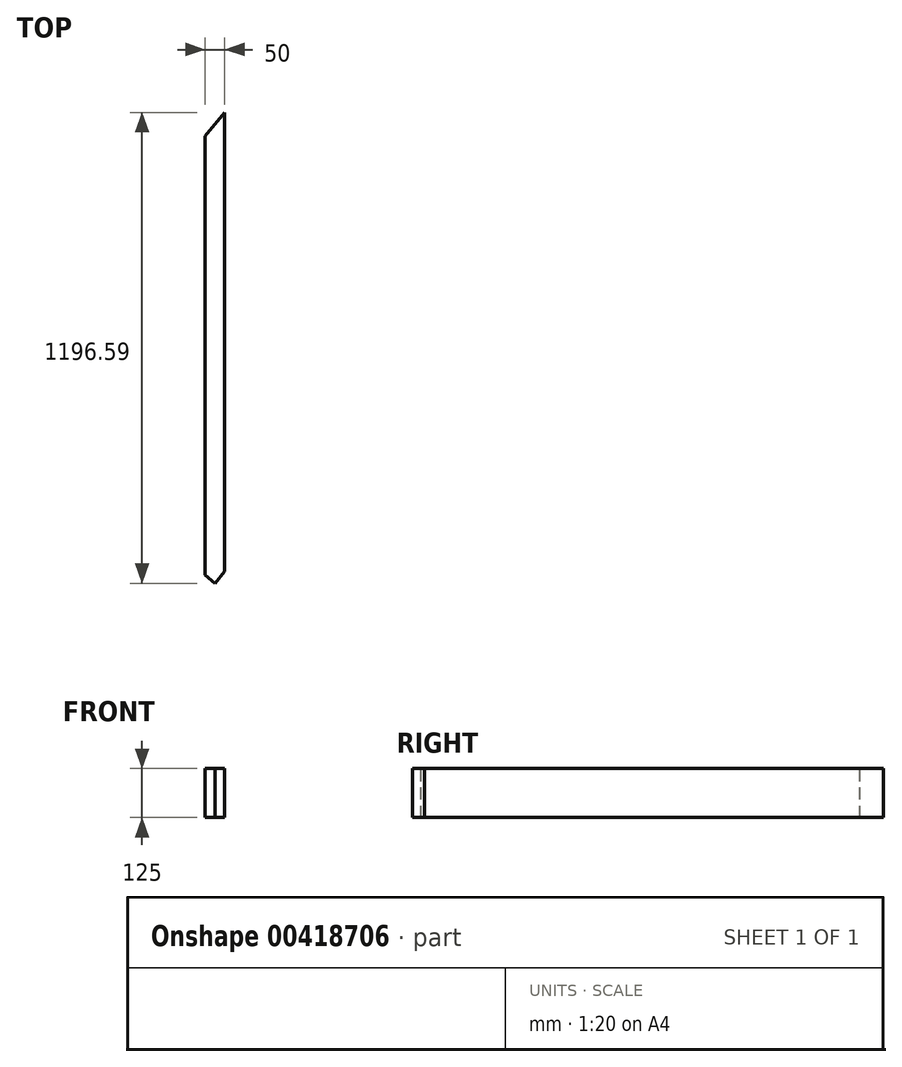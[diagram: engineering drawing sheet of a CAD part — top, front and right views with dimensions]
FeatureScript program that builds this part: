
annotation { "Feature Type Name" : "Feature", "Feature Type Description" : "" }
export const myFeature = defineFeature(function(context is Context, id is Id, definition is map)
    precondition{}
    {
        {
            var Q0;
            Q0=qCreatedBy(makeId("Front.planeOp"),FACE);
            var sketch = newSketch(context, id + "F0", { "sketchPlane" : qUnion([Q0])});
            skLineSegment(sketch, "E0.bottom", {"start": v(25, 62.5) * mm, "end": v(-25, 62.5) * mm});
            skLineSegment(sketch, "E0.top", {"start": v(25, -62.5) * mm, "end": v(-25, -62.5) * mm});
            skLineSegment(sketch, "E0.left", {"start": v(25, 62.5) * mm, "end": v(25, -62.5) * mm});
            skLineSegment(sketch, "E0.right", {"start": v(-25, 62.5) * mm, "end": v(-25, -62.5) * mm});
            skPoint(sketch, "E0.middle", {"position": v(0, 0) * mm});
            skSolve(sketch);
        }
        {
            var Q0;
            Q0 = qSketchRegion(id + "F0", true);
            extrude(context, id + "F1", {"entities" : qUnion([Q0]), "depth" : 1200 * mm});
        }
        {
            var Q0;
            Q0=makeQuery(id+"F1.opExtrude","SWEPT_FACE",FACE,{"disambiguationData":[OSD([sQuery(id+"F0.wireOp",EDGE,"E0.bottom")])]});
            var sketch = newSketch(context, id + "F2", { "sketchPlane" : qUnion([Q0])});
            skLineSegment(sketch, "E1", {"start": v(25, 0) * mm, "end": v(-25, -59.59) * mm});
            skLineSegment(sketch, "E2", {"start": v(-25, -59.59) * mm, "end": v(-25, 0) * mm});
            skLineSegment(sketch, "E3", {"start": v(-25, 0) * mm, "end": v(25, 0) * mm});
            skSolve(sketch);
        }
        {
            var Q0;
            Q0 = qSketchRegion(id + "F2", true);
            extrude(context, id + "F3", {"entities" : qUnion([Q0]), "operationType" : NewBodyOperationType.REMOVE, "endBound" : BoundingType.UP_TO_NEXT, "oppositeDirection" : true, "depth" : 25 * mm});
        }
        {
            var Q0;
            Q0=makeQuery(id+"F1.opExtrude","SWEPT_FACE",FACE,{"disambiguationData":[OSD([sQuery(id+"F0.wireOp",EDGE,"E0.bottom")])]});
            var sketch = newSketch(context, id + "F4", { "sketchPlane" : qUnion([Q0])});
            skLineSegment(sketch, "E4", {"start": v(-25, -1175.6) * mm, "end": v(-25, -1200) * mm});
            skLineSegment(sketch, "E5", {"start": v(-25, -1200) * mm, "end": v(25, -1200) * mm});
            skLineSegment(sketch, "E6", {"start": v(25, -1200) * mm, "end": v(25, -1166.8) * mm});
            skLineSegment(sketch, "E7", {"start": v(-25, -1175.6) * mm, "end": v(0, -1196.59) * mm});
            skLineSegment(sketch, "E8", {"start": v(0, -1196.59) * mm, "end": v(25, -1166.8) * mm});
            skSolve(sketch);
        }
        {
            var Q0;
            Q0 = qSketchRegion(id + "F4", true);
            extrude(context, id + "F5", {"entities" : qUnion([Q0]), "operationType" : NewBodyOperationType.REMOVE, "endBound" : BoundingType.UP_TO_NEXT, "oppositeDirection" : true, "depth" : 25 * mm});
        }
    });
